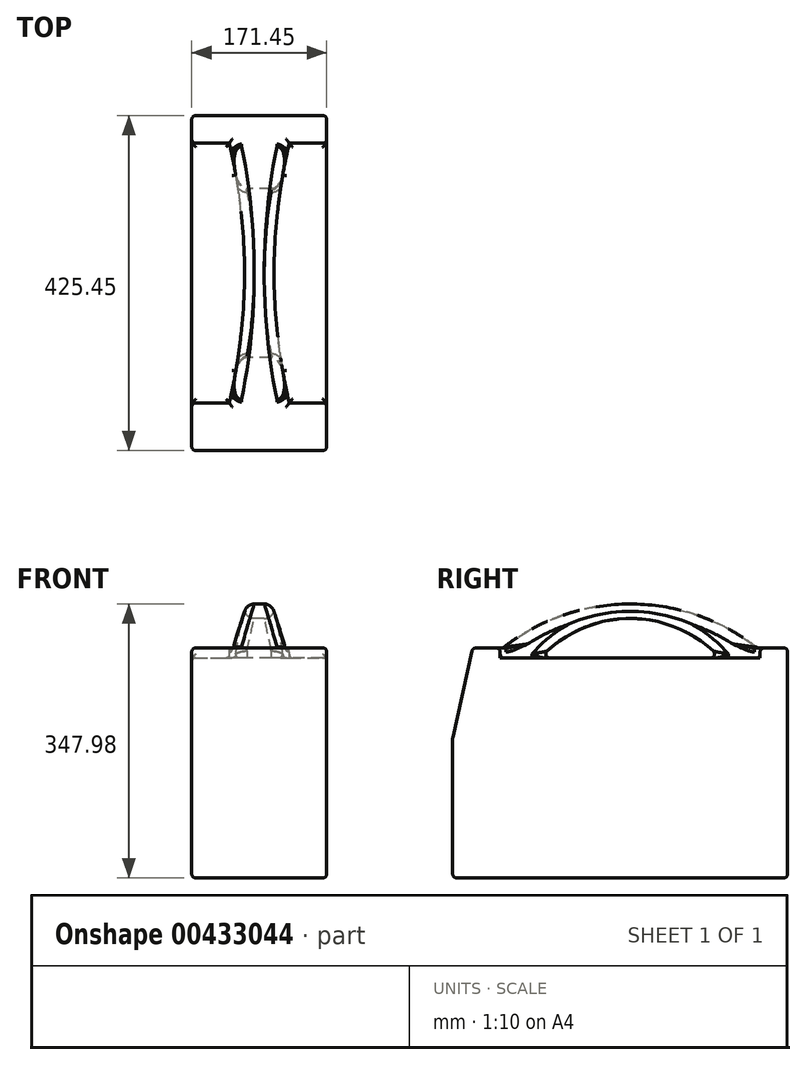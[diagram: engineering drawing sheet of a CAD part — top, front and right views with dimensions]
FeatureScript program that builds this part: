
annotation { "Feature Type Name" : "Feature", "Feature Type Description" : "" }
export const myFeature = defineFeature(function(context is Context, id is Id, definition is map)
    precondition{}
    {
        {
            var Q0;
            Q0=qCreatedBy(makeId("Right.planeOp"),FACE);
            var sketch = newSketch(context, id + "F0", { "sketchPlane" : qUnion([Q0])});
            skLineSegment(sketch, "E0.bottom", {"start": v(0, 0) * mm, "end": v(-425.45, 0) * mm});
            skLineSegment(sketch, "E0.left", {"start": v(0, 0) * mm, "end": v(0, 292.1) * mm});
            skLineSegment(sketch, "E1", {"start": v(0, 292.1) * mm, "end": v(-38.1, 292.1) * mm});
            skLineSegment(sketch, "E2", {"start": v(-85.73, 279.4) * mm, "end": v(-314.33, 279.4) * mm});
            skArc(sketch, "E3", {"start": v(-38.1, 292.1) * mm, "mid": v(-200.02, 347.98) * mm, "end": v(-361.95, 292.1) * mm});
            skArc(sketch, "E4", {"start": v(-85.73, 279.4) * mm, "mid": v(-200.03, 329.59) * mm, "end": v(-314.33, 279.4) * mm});
            skPoint(sketch, "E5", {"position": v(-212.73, 0) * mm});
            skLineSegment(sketch, "E6", {"start": v(-425.45, 0) * mm, "end": v(-425.45, 177.8) * mm});
            skLineSegment(sketch, "E7", {"start": v(-425.45, 177.8) * mm, "end": v(-400.05, 292.1) * mm});
            skLineSegment(sketch, "E8", {"start": v(-400.05, 292.1) * mm, "end": v(-361.95, 292.1) * mm});
            skSolve(sketch);
        }
        {
            var Q0;
            Q0=makeQuery(id+"F0.imprint","IMPRINT",FACE,{"disambiguationData":[TD([[makeQuery(id+"F0.imprint","IMPRINT",EDGE,{"derivedFrom":sQuery(id+"F0.wireOp",EDGE,"E0.bottom")}),-1.0]])]});
            extrude(context, id + "F1", {"entities" : qUnion([Q0]), "depth" : 171.45 * mm});
        }
        {
            var Q0;
            Q0=makeQuery(id+"F1.opExtrude","SWEPT_FACE",FACE,{"disambiguationData":[OSD([sQuery(id+"F0.wireOp",EDGE,"E2")])]});
            var sketch = newSketch(context, id + "F2", { "sketchPlane" : qUnion([Q0])});
            skLineSegment(sketch, "E9", {"start": v(0, -365.13) * mm, "end": v(0, -34.92) * mm});
            skLineSegment(sketch, "E10", {"start": v(0, -34.92) * mm, "end": v(47.63, -34.92) * mm});
            skLineSegment(sketch, "E11", {"start": v(123.83, -34.92) * mm, "end": v(171.45, -34.92) * mm});
            skLineSegment(sketch, "E12", {"start": v(171.45, -34.92) * mm, "end": v(171.45, -365.12) * mm});
            skLineSegment(sketch, "E13", {"start": v(171.45, -365.12) * mm, "end": v(123.83, -365.12) * mm});
            skLineSegment(sketch, "E14", {"start": v(0, -365.13) * mm, "end": v(47.63, -365.13) * mm});
            skArc(sketch, "E15", {"start": v(123.83, -34.93) * mm, "mid": v(104.78, -200.02) * mm, "end": v(123.83, -365.12) * mm});
            skArc(sketch, "E16", {"start": v(47.62, -365.12) * mm, "mid": v(66.67, -200.02) * mm, "end": v(47.62, -34.93) * mm});
            skSolve(sketch);
        }
        {
            var Q0;
            {var subQ5=sQuery(id+"F2.wireOp",EDGE,"E14");Q0=makeQuery(id+"F2.imprint","IMPRINT",FACE,{"disambiguationData":[TD([[makeQuery(id+"F2.imprint","IMPRINT",EDGE,{"derivedFrom":subQ5}),1.0]])]});}
            var Q1;
            {var subQ0=sQuery(id+"F2.wireOp",EDGE,"E9");var subQ1=sQuery(id+"F0.wireOp",EDGE,"E4");var subQ2=sQuery(id+"F0.wireOp",EDGE,"E2");var subQ3=makeQuery(id+"F1.opExtrude","SWEPT_EDGE",EDGE,{"disambiguationData":[OSD([subQ2,subQ1]),TDD([makeQuery(id+"F0.imprint","INTERSECT",VERTEX,{"disambiguationData":[OD(0.0)],"derivedFrom":[subQ2,subQ1]})])]});var subQ4=makeQuery(id+"F2.imprint","INTERSECT",VERTEX,{"derivedFrom":[subQ3,subQ0]});var subQ5=makeQuery(id+"F1.opExtrude","SWEPT_EDGE",EDGE,{"disambiguationData":[OSD([subQ2,subQ1]),TDD([makeQuery(id+"F0.imprint","INTERSECT",VERTEX,{"disambiguationData":[OD(1.0)],"derivedFrom":[subQ2,subQ1]})])]});var subQ6=makeQuery(id+"F2.imprint","INTERSECT",VERTEX,{"derivedFrom":[subQ5,subQ0]});Q1=makeQuery(id+"F2.imprint","IMPRINT",FACE,{"disambiguationData":[TD([[makeQuery(id+"F2.imprint","IMPRINT",EDGE,{"disambiguationData":[TD([[subQ4,-1.0],[subQ6,1.0]])],"derivedFrom":subQ0}),1.0]])]});}
            var Q2;
            {var subQ5=sQuery(id+"F2.wireOp",EDGE,"E10");Q2=makeQuery(id+"F2.imprint","IMPRINT",FACE,{"disambiguationData":[TD([[makeQuery(id+"F2.imprint","IMPRINT",EDGE,{"derivedFrom":subQ5}),-1.0]])]});}
            var Q3;
            {var subQ0=sQuery(id+"F2.wireOp",EDGE,"E11");Q3=makeQuery(id+"F2.imprint","IMPRINT",FACE,{"disambiguationData":[TD([[makeQuery(id+"F2.imprint","IMPRINT",EDGE,{"derivedFrom":subQ0}),-1.0]])]});}
            var Q4;
            {var subQ0=sQuery(id+"F2.wireOp",EDGE,"E12");var subQ1=sQuery(id+"F0.wireOp",EDGE,"E4");var subQ2=sQuery(id+"F0.wireOp",EDGE,"E2");var subQ3=makeQuery(id+"F1.opExtrude","SWEPT_EDGE",EDGE,{"disambiguationData":[OSD([subQ2,subQ1]),TDD([makeQuery(id+"F0.imprint","INTERSECT",VERTEX,{"disambiguationData":[OD(0.0)],"derivedFrom":[subQ2,subQ1]})])]});var subQ4=makeQuery(id+"F2.imprint","INTERSECT",VERTEX,{"derivedFrom":[subQ3,subQ0]});Q4=makeQuery(id+"F2.imprint","IMPRINT",FACE,{"disambiguationData":[TD([[makeQuery(id+"F2.imprint","IMPRINT",EDGE,{"disambiguationData":[TD([[subQ4,-1.0]])],"derivedFrom":subQ0}),-1.0]])]});}
            var Q5;
            {var subQ5=sQuery(id+"F2.wireOp",EDGE,"E13");Q5=makeQuery(id+"F2.imprint","IMPRINT",FACE,{"disambiguationData":[TD([[makeQuery(id+"F2.imprint","IMPRINT",EDGE,{"derivedFrom":subQ5}),-1.0]])]});}
            extrude(context, id + "F3", {"entities" : qUnion([Q0, Q1, Q2, Q3, Q4, Q5]), "operationType" : NewBodyOperationType.REMOVE, "endBound" : BoundingType.THROUGH_ALL, "depth" : 25.4 * mm});
        }
        {
            var Q0;
            Q0=makeQuery(id+"F3.boolean.opBoolean","INTERSECT",EDGE,{"derivedFrom":[makeQuery(id+"F1.opExtrude","SWEPT_FACE",FACE,{"disambiguationData":[OSD([sQuery(id+"F0.wireOp",EDGE,"E3")])]}),makeQuery(id+"F3.opExtrude","SWEPT_FACE",FACE,{"disambiguationData":[OSD([sQuery(id+"F2.wireOp",EDGE,"E16")])]})]});
            var Q1;
            Q1=makeQuery(id+"F3.boolean.opBoolean","INTERSECT",EDGE,{"derivedFrom":[makeQuery(id+"F1.opExtrude","SWEPT_FACE",FACE,{"disambiguationData":[OSD([sQuery(id+"F0.wireOp",EDGE,"E3")])]}),makeQuery(id+"F3.opExtrude","SWEPT_FACE",FACE,{"disambiguationData":[OSD([sQuery(id+"F2.wireOp",EDGE,"E15")])]})]});
            var Q2;
            Q2=makeQuery(id+"F3.boolean.opBoolean","INTERSECT",EDGE,{"derivedFrom":[makeQuery(id+"F1.opExtrude","SWEPT_FACE",FACE,{"disambiguationData":[OSD([sQuery(id+"F0.wireOp",EDGE,"E4")])]}),makeQuery(id+"F3.opExtrude","SWEPT_FACE",FACE,{"disambiguationData":[OSD([sQuery(id+"F2.wireOp",EDGE,"E16")])]})]});
            var Q3;
            Q3=makeQuery(id+"F3.boolean.opBoolean","INTERSECT",EDGE,{"derivedFrom":[makeQuery(id+"F1.opExtrude","SWEPT_FACE",FACE,{"disambiguationData":[OSD([sQuery(id+"F0.wireOp",EDGE,"E4")])]}),makeQuery(id+"F3.opExtrude","SWEPT_FACE",FACE,{"disambiguationData":[OSD([sQuery(id+"F2.wireOp",EDGE,"E15")])]})]});
            fillet(context, id + "F4", {"entities" : qUnion([Q0, Q1, Q2, Q3]), "radius" : 12.7 * mm, "tangentPropagation" : true, "allowEdgeOverflow" : false});
        }
        {
            var Q0;
            Q0=makeQuery(id+"F1.opExtrude","CAP_FACE",FACE,{"disambiguationData":[OSD([sQuery(id+"F0.wireOp",EDGE,"E0.bottom"),sQuery(id+"F0.wireOp",EDGE,"E0.left"),sQuery(id+"F0.wireOp",EDGE,"E1"),sQuery(id+"F0.wireOp",EDGE,"E2"),sQuery(id+"F0.wireOp",EDGE,"E3"),sQuery(id+"F0.wireOp",EDGE,"E4"),sQuery(id+"F0.wireOp",EDGE,"E6"),sQuery(id+"F0.wireOp",EDGE,"E7"),sQuery(id+"F0.wireOp",EDGE,"E8")])],"isStart":true});
            var Q1;
            Q1=makeQuery(id+"F1.opExtrude","SWEPT_FACE",FACE,{"disambiguationData":[OSD([sQuery(id+"F0.wireOp",EDGE,"E7")])]});
            var Q2;
            Q2=makeQuery(id+"F1.opExtrude","SWEPT_FACE",FACE,{"disambiguationData":[OSD([sQuery(id+"F0.wireOp",EDGE,"E6")])]});
            var Q3;
            Q3=makeQuery(id+"F1.opExtrude","SWEPT_FACE",FACE,{"disambiguationData":[OSD([sQuery(id+"F0.wireOp",EDGE,"E0.bottom")])]});
            var Q4;
            Q4=makeQuery(id+"F1.opExtrude","SWEPT_FACE",FACE,{"disambiguationData":[OSD([sQuery(id+"F0.wireOp",EDGE,"E0.left")])]});
            var Q5;
            Q5=makeQuery(id+"F1.opExtrude","CAP_FACE",FACE,{"disambiguationData":[OSD([sQuery(id+"F0.wireOp",EDGE,"E0.bottom"),sQuery(id+"F0.wireOp",EDGE,"E0.left"),sQuery(id+"F0.wireOp",EDGE,"E1"),sQuery(id+"F0.wireOp",EDGE,"E2"),sQuery(id+"F0.wireOp",EDGE,"E3"),sQuery(id+"F0.wireOp",EDGE,"E4"),sQuery(id+"F0.wireOp",EDGE,"E6"),sQuery(id+"F0.wireOp",EDGE,"E7"),sQuery(id+"F0.wireOp",EDGE,"E8")])],"isStart":false});
            var Q6;
            Q6=makeQuery(id+"F1.opExtrude","SWEPT_FACE",FACE,{"disambiguationData":[OSD([sQuery(id+"F0.wireOp",EDGE,"E8")])]});
            var Q7;
            Q7=makeQuery(id+"F1.opExtrude","SWEPT_FACE",FACE,{"disambiguationData":[OSD([sQuery(id+"F0.wireOp",EDGE,"E1")])]});
            var Q8;
            Q8=makeQuery(id+"F3.boolean.opBoolean","MERGE",FACE,{"derivedFrom":[makeQuery(id+"F1.opExtrude","SWEPT_FACE",FACE,{"disambiguationData":[OSD([sQuery(id+"F0.wireOp",EDGE,"E2")])]}),makeQuery(id+"F3.opExtrude","CAP_FACE",FACE,{"disambiguationData":[OSD([sQuery(id+"F2.wireOp",EDGE,"E9"),sQuery(id+"F2.wireOp",EDGE,"E10"),sQuery(id+"F2.wireOp",EDGE,"E14"),sQuery(id+"F2.wireOp",EDGE,"E16")])],"isStart":true}),makeQuery(id+"F3.opExtrude","CAP_FACE",FACE,{"disambiguationData":[OSD([sQuery(id+"F2.wireOp",EDGE,"E11"),sQuery(id+"F2.wireOp",EDGE,"E12"),sQuery(id+"F2.wireOp",EDGE,"E13"),sQuery(id+"F2.wireOp",EDGE,"E15")])],"isStart":true})]});
            fillet(context, id + "F5", {"entities" : qUnion([Q0, Q1, Q2, Q3, Q4, Q5, Q6, Q7, Q8]), "radius" : 5.08 * mm, "tangentPropagation" : true, "allowEdgeOverflow" : false});
        }
    });
